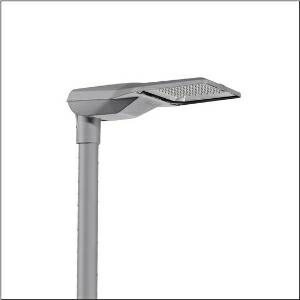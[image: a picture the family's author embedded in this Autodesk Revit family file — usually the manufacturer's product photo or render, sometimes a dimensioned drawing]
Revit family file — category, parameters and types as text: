
# Revit family: streetlight_sl_21_iq_midi___p0_5a_5xe3v31g08nb_569c
name_source: partatom
category: Lighting Fixtures
units: mm (PartAtom-declared; Revit-internal decimal feet)

## family parameters
Cut with Voids When Loaded = No
Host = Face
Light Source = No
Part Type = Normal
Room Calculation Point = No
Round Connector Dimension = Use Diameter
Shared = No

## types (1)
- --- (1 x LED, 22830 lm, 155.5 W, 3000K)
    Apparent Load = 155 VA
    CIE Flux Codes = 37 73 96 100 100
    Color Rendering = 70
    Color Temperature = 3000K
    Default Elevation = 1800 mm
    Description = Streetlight SL 21 iQ midi, mast luminaire, primary light control with lens, of PMMA, primary optical cover: cover, of toughened safety glass, transparent, light distribution: P0.5a, light emission: direct distribution, primary light characteristic: asymmetric, installation type: post-top, side-entry, LED, High Power LED, rated luminous flux: 22.830lm, luminous efficacy: 147lm/W, light colour: 730, colour temperature: 3000K, control gear: iQ Street-Remote, control: pre-setting: linear dimming characteristic, Street-Remote, Auto-Match, Temp-Guard, Lumen-Switch, Night-Set, Smart-Wire, Light-Fading, Desk-Remote (wireless, voltage-free reading and setting of iQ features in the workshop via application-optimized NFC function/RFID function), optimised constant luminous flux control (CLO 2.0), mains connection: 230..240V, AC, 50/60Hz, start of lifetime: 156W, end of service life: 162W, reduction: 69W, luminaire housing, of diecast aluminium, powder-coated, Siteco® metallic grey (DB 702S), corrosivity category C5 mid according to DIN EN ISO 12944, please order mast flange separately, inclination adjustable: 0°, 5°, 10°, 15°, sealing non-destructively replaceable, multi-level sealing system, length: 644mm, width: 335mm, height: 110mm, mast flange for spigot size: 42mm (side-entry): 5XC10008XM4, 60/48mm (side-entry/post-top): 5XC10108XM2, 76/60mm (side-entry/post-top): 5XC10108XM1, mounting height: 4..8m, protection rating (complete): IP66, insulation class (complete): insulation class II (safety insulation), certification: CE, ENEC, ENEC+, VDE, impact resistance: IK10, permissible operating ambient temperature for outdoor applications: -40..+50°C, standard-compliant lighting for roads and squares, packaging unit: 1 piece

Light Distribution: P0.5a
    Height = 111 mm
    Lamp = 1 x LED
    Lamp Light Flux = 22830 lm
    Lamp Power = 155.5 W
    Lamp count = 1
    Length = 644 mm
    Luminous efficacy = 147 lm/W
    Manufacturer = Siteco
    ModVariant = No
    Model = 5XE3V31G08NB
    Number of Poles = 1
    OnlyDefault = Yes
    Power Factor = 1
    Product Name = Streetlight SL 21 iQ midi | P0.5a
    Product group = mast luminaire | pylon top
    ProductGroupID = 6100
    Protection Class = Protection class II
    Protection Degree = IP 66
    RLX_Detail_Level = 1
    RLX_Emergency_Light_Flux = 0 lm
    RLX_Emergency_Type = 0
    RLX_Emergency_Type_DB = No
    RlxData = <blob elided: 26909 chars, md5=0af18f1b>
    Socket = socket
    Standby Power = 0 W
    System Light Flux = 22831 lm
    System Power = 155 W
    Type Comments = factory setting: luminous flux: 100 % | dim-lin: 254 | 823 mA
    Type Image = l_1004298.jpg
    URL = http://relux.com
    VarID = @adj_069118
    Voltage = 0 V
    Weight = 0.00 kg
    Width = 336 mm

## geometry (parser evidence)
native form markers: Blend x4, Sweep x10
no freeform markers — native parametric forms only
